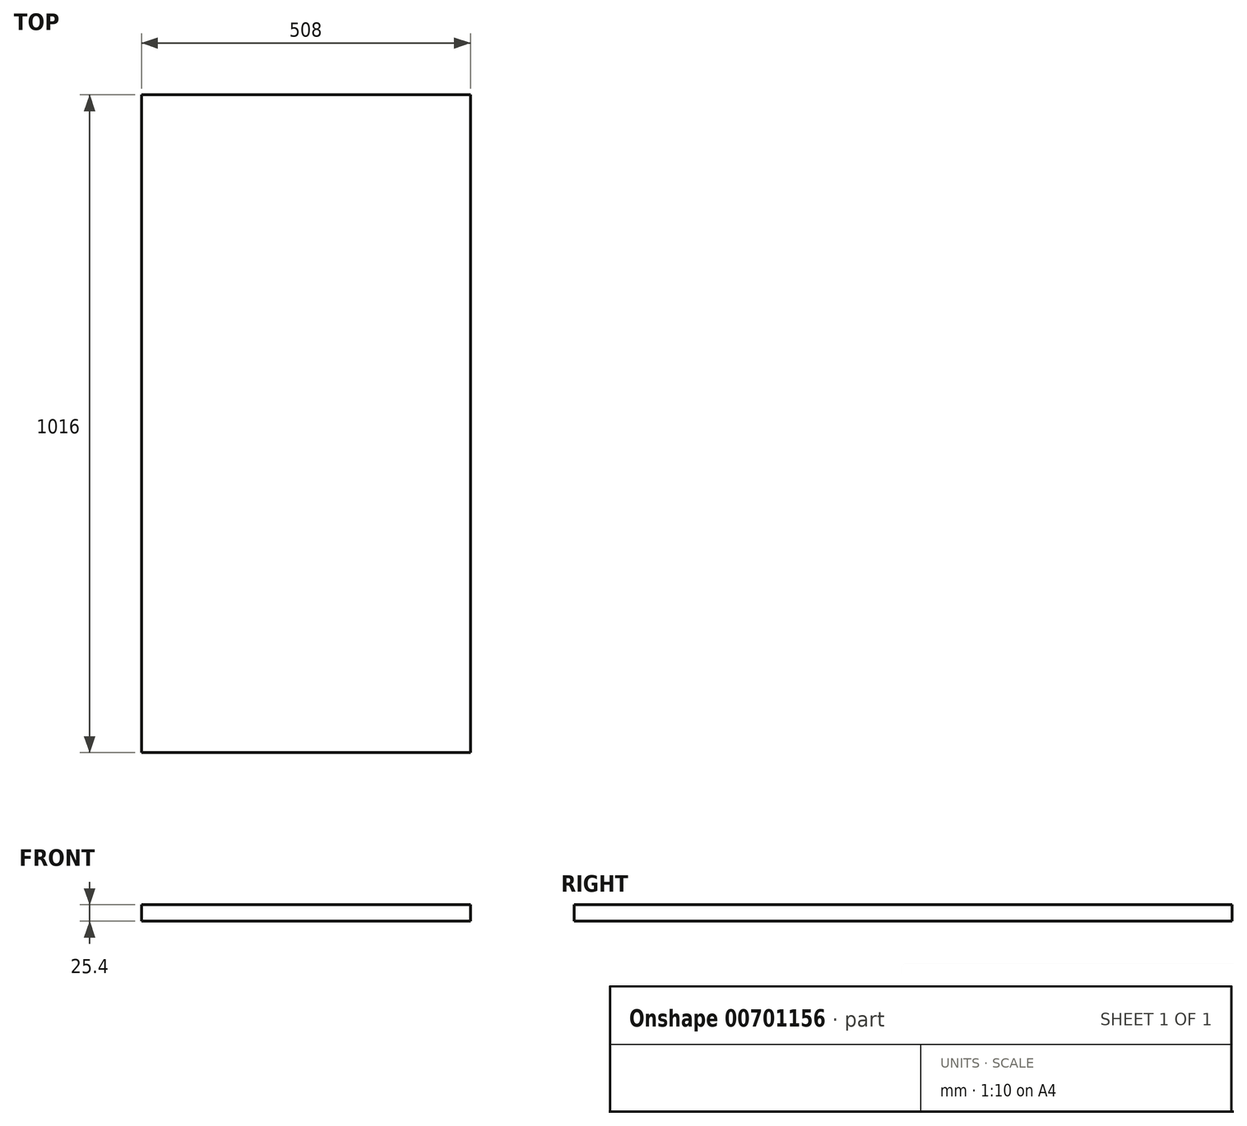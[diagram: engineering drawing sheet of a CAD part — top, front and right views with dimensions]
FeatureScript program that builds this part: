
annotation { "Feature Type Name" : "Feature", "Feature Type Description" : "" }
export const myFeature = defineFeature(function(context is Context, id is Id, definition is map)
    precondition{}
    {
        {
            var Q0;
            Q0=qCreatedBy(makeId("Top.planeOp"),FACE);
            var sketch = newSketch(context, id + "F0", { "sketchPlane" : qUnion([Q0])});
            skLineSegment(sketch, "E0.bottom", {"start": v(-254, 508) * mm, "end": v(254, 508) * mm});
            skLineSegment(sketch, "E0.top", {"start": v(-254, -508) * mm, "end": v(254, -508) * mm});
            skLineSegment(sketch, "E0.left", {"start": v(-254, 508) * mm, "end": v(-254, -508) * mm});
            skLineSegment(sketch, "E0.right", {"start": v(254, 508) * mm, "end": v(254, -508) * mm});
            skPoint(sketch, "E0.middle", {"position": v(0, 0) * mm});
            skSolve(sketch);
        }
        {
            var Q0;
            Q0 = qSketchRegion(id + "F0", true);
            extrude(context, id + "F1", {"entities" : qUnion([Q0]), "depth" : 25.4 * mm, "offsetDistance" : 25.4 * mm});
        }
    });
